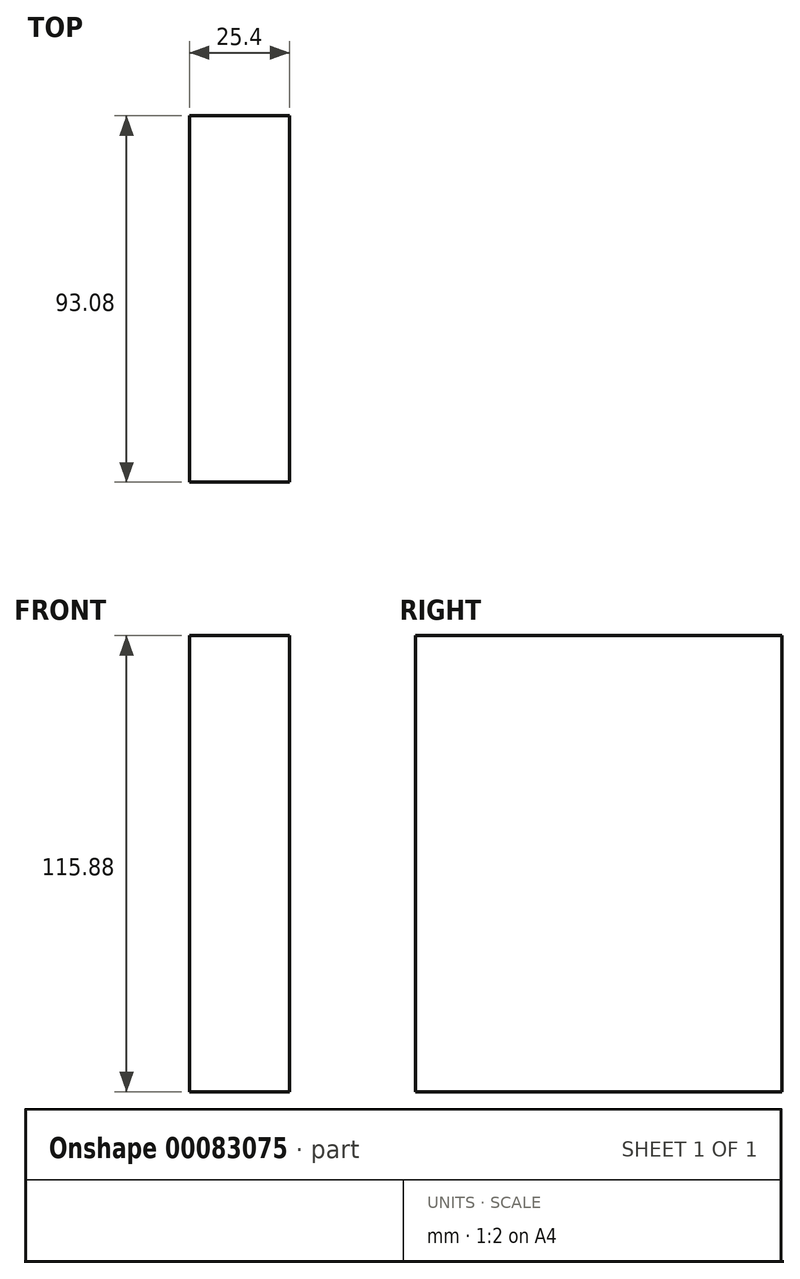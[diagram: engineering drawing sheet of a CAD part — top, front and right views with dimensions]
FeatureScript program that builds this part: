
annotation { "Feature Type Name" : "Feature", "Feature Type Description" : "" }
export const myFeature = defineFeature(function(context is Context, id is Id, definition is map)
    precondition{}
    {
        {
            var Q0;
            Q0=qCreatedBy(makeId("Right.planeOp"),FACE);
            var sketch = newSketch(context, id + "F0", { "sketchPlane" : qUnion([Q0])});
            skLineSegment(sketch, "E0.bottom", {"start": v(-26.59, -57.94) * mm, "end": v(66.49, -57.94) * mm});
            skLineSegment(sketch, "E0.top", {"start": v(-26.59, 57.94) * mm, "end": v(66.49, 57.94) * mm});
            skLineSegment(sketch, "E0.left", {"start": v(-26.59, -57.94) * mm, "end": v(-26.59, 57.94) * mm});
            skLineSegment(sketch, "E0.right", {"start": v(66.49, -57.94) * mm, "end": v(66.49, 57.94) * mm});
            skPoint(sketch, "E0.middle", {"position": v(19.95, 0) * mm});
            skSolve(sketch);
        }
        {
            var Q0;
            Q0 = qSketchRegion(id + "F0", true);
            extrude(context, id + "F1", {"entities" : qUnion([Q0]), "depth" : 25.4 * mm});
        }
    });
